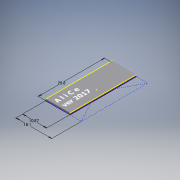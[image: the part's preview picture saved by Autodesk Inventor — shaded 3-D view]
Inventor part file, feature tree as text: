
AUTODESK INVENTOR PART (.ipt)
format: ipt  version: 2016 (Build 200138000, 138)  size: 104,448 bytes
history: native  units: mm
features: sketch x2, other x1, extrude x1
ambient origin geometry x8: Origin, YZ Plane, XZ Plane, XY Plane, X Axis, Y Axis, Z Axis, Center Point
bodies: Body1 (feature_tree)
feature tree (4):
  other  "ソリッド1"
  extrude  "押し出し1"  Depth=16.1mm
  sketch  "スケッチ3"
  sketch  "スケッチ1"
